# Revit family: Clarus_Flex Wall_R19
name_source: partatom
category: Furniture
units: mm (PartAtom-declared; Revit-internal decimal feet)

## family parameters
Cut with Voids When Loaded = No
Host = Face
Room Calculation Point = No
Shared = No

## types (2) — shared parameters
Default Elevation = 0"
Depth = 22"
Description = Flex Wall is a free-standing glassboard wall system with a fully integrated, omnidirectional wheel system built into the base. The wheel system allows Flex to roll easily from room to room — then, this award-winning, revolutionary design seamlessly transforms into a fixed, free-standing, wall partition.
Height = 78"
Manufacturer = Clarus
Model = Flex Wall
Modeled By = Commense Studio
Product URL = https://www.clarus.com
URL = https://www.clarus.com

## per-type parameters (varying)
| type | Width |
| Mediium 40" X 78" X 22" | 40" |
| Large 60" X 78" X 22" | 60" |

## geometry (parser evidence)
native form markers: Blend x29, Sweep x6
no freeform markers — native parametric forms only
